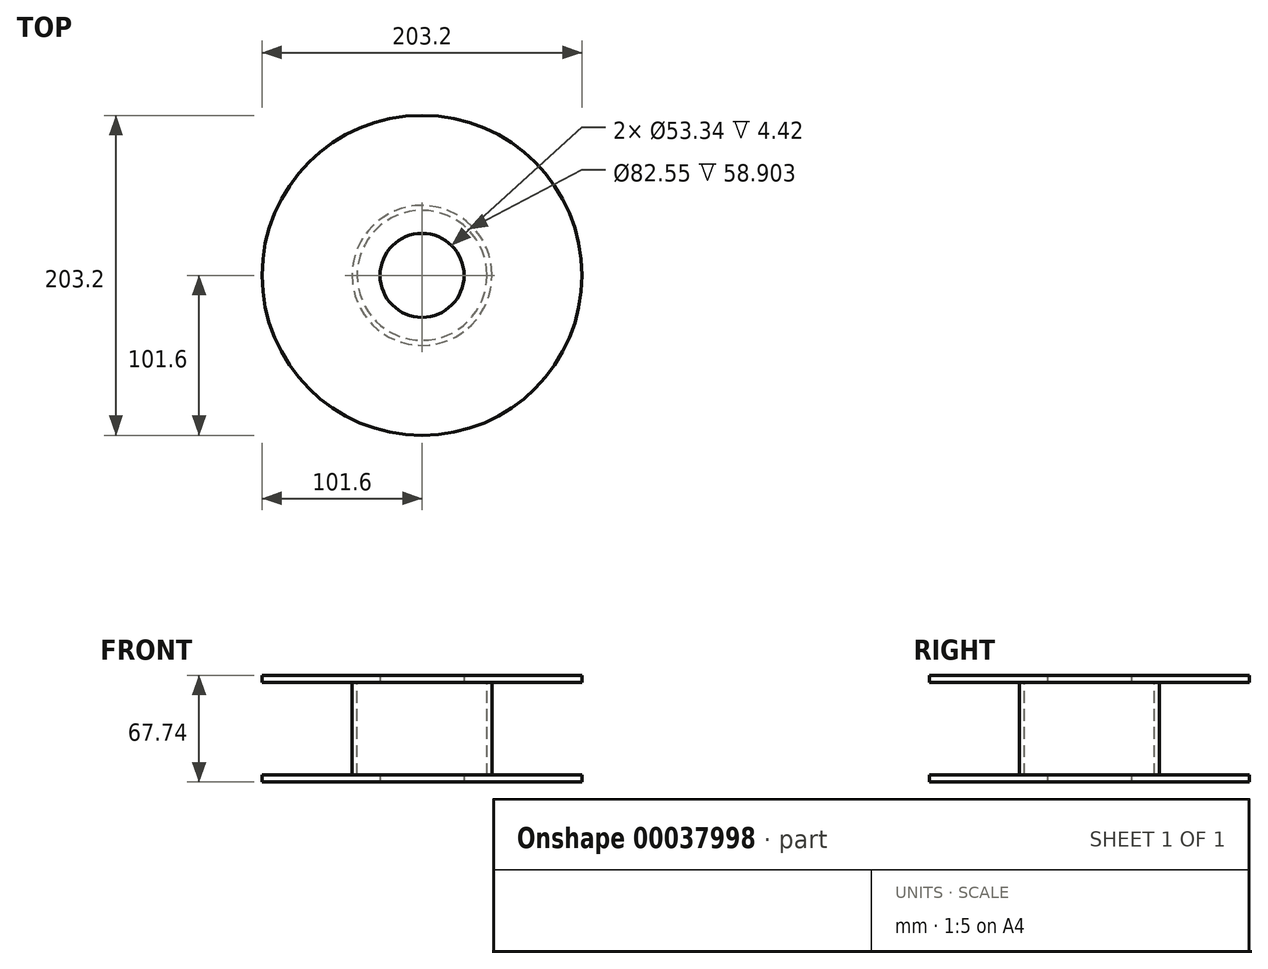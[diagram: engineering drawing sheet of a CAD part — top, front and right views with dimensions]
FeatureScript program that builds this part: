
annotation { "Feature Type Name" : "Feature", "Feature Type Description" : "" }
export const myFeature = defineFeature(function(context is Context, id is Id, definition is map)
    precondition{}
    {
        {
            var Q0;
            Q0=qCreatedBy(makeId("Top.planeOp"),FACE);
            var sketch = newSketch(context, id + "F0", { "sketchPlane" : qUnion([Q0])});
            skCircle(sketch, "E0", {"center": v(0, 0) * mm, "radius": 26.67 * mm});
            skCircle(sketch, "E1", {"center": v(0, 0) * mm, "radius": 101.6 * mm});
            skSolve(sketch);
        }
        {
            var Q0;
            Q0=makeQuery(id+"F0.imprint","IMPRINT",FACE,{"disambiguationData":[TD([[makeQuery(id+"F0.imprint","IMPRINT",EDGE,{"derivedFrom":sQuery(id+"F0.wireOp",EDGE,"E0")}),-1.0]])]});
            extrude(context, id + "F1", {"entities" : qUnion([Q0]), "depth" : 4.42 * mm});
        }
        {
            var Q0;
            Q0=makeQuery(id+"F1.opExtrude","CAP_FACE",FACE,{"disambiguationData":[OSD([sQuery(id+"F0.wireOp",EDGE,"E0"),sQuery(id+"F0.wireOp",EDGE,"E1")])],"isStart":false});
            var sketch = newSketch(context, id + "F2", { "sketchPlane" : qUnion([Q0])});
            skCircle(sketch, "E2", {"center": v(0, 0) * mm, "radius": 44.45 * mm});
            skSolve(sketch);
        }
        {
            var Q0;
            Q0=makeQuery(id+"F2.imprint","IMPRINT",FACE,{"disambiguationData":[TD([[makeQuery(id+"F2.imprint","IMPRINT",EDGE,{"derivedFrom":sQuery(id+"F2.wireOp",EDGE,"E2")}),1.0]])]});
            extrude(context, id + "F3", {"entities" : qUnion([Q0]), "operationType" : NewBodyOperationType.ADD, "depth" : 58.9 * mm});
        }
        {
            var Q0;
            Q0=makeQuery(id+"F3.opExtrude","CAP_FACE",FACE,{"disambiguationData":[OSD([sQuery(id+"F0.wireOp",EDGE,"E0"),sQuery(id+"F2.wireOp",EDGE,"E2")])],"isStart":false});
            var sketch = newSketch(context, id + "F4", { "sketchPlane" : qUnion([Q0])});
            skCircle(sketch, "E3", {"center": v(0, 0) * mm, "radius": 41.28 * mm});
            skLineSegment(sketch, "E4", {"start": v(-44.45, 0) * mm, "end": v(-41.28, 0) * mm});
            skLineSegment(sketch, "E5", {"start": v(0, 0) * mm, "end": v(-41.28, 0) * mm});
            skSolve(sketch);
        }
        {
            var Q0;
            Q0=qSketchRegion(id+"F4",true);
            var Q1;
            Q1=makeQuery(id+"F1.opExtrude","CAP_FACE",FACE,{"disambiguationData":[OSD([sQuery(id+"F0.wireOp",EDGE,"E0"),sQuery(id+"F0.wireOp",EDGE,"E1")])],"isStart":false});
            extrude(context, id + "F5", {"entities" : qUnion([Q0]), "operationType" : NewBodyOperationType.REMOVE, "endBound" : BoundingType.UP_TO_SURFACE, "oppositeDirection" : true, "endBoundEntityFace" : qUnion([Q1]), "depth" : 25.4 * mm});
        }
        {
            var Q0;
            Q0=makeQuery(id+"F3.opExtrude","CAP_FACE",FACE,{"disambiguationData":[OSD([sQuery(id+"F0.wireOp",EDGE,"E0"),sQuery(id+"F2.wireOp",EDGE,"E2")])],"isStart":false});
            var sketch = newSketch(context, id + "F6", { "sketchPlane" : qUnion([Q0])});
            skCircle(sketch, "E6", {"center": v(0, 0) * mm, "radius": 101.6 * mm});
            skCircle(sketch, "E7", {"center": v(0, 0) * mm, "radius": 26.67 * mm});
            skSolve(sketch);
        }
        {
            var Q0;
            {var subQ0=makeQuery(id+"F6.imprint","IMPRINT",EDGE,{"derivedFrom":makeQuery(id+"F3.opExtrude","CAP_EDGE",EDGE,{"disambiguationData":[OSD([sQuery(id+"F2.wireOp",EDGE,"E2")])],"isStart":false})});Q0=qUnion([makeQuery(id+"F6.imprint","IMPRINT",FACE,{"disambiguationData":[TD([[makeQuery(id+"F6.imprint","IMPRINT",EDGE,{"derivedFrom":sQuery(id+"F6.wireOp",EDGE,"E6")}),1.0]])]}),makeQuery(id+"F6.imprint","IMPRINT",FACE,{"disambiguationData":[TD([[makeQuery(id+"F6.imprint","IMPRINT",EDGE,{"derivedFrom":sQuery(id+"F6.wireOp",EDGE,"E7")}),-1.0]])]}),makeQuery(id+"F6.imprint","IMPRINT",FACE,{"disambiguationData":[TD([[subQ0,1.0]])]})]);}
            extrude(context, id + "F7", {"entities" : qUnion([Q0]), "operationType" : NewBodyOperationType.ADD, "depth" : 4.42 * mm});
        }
    });
